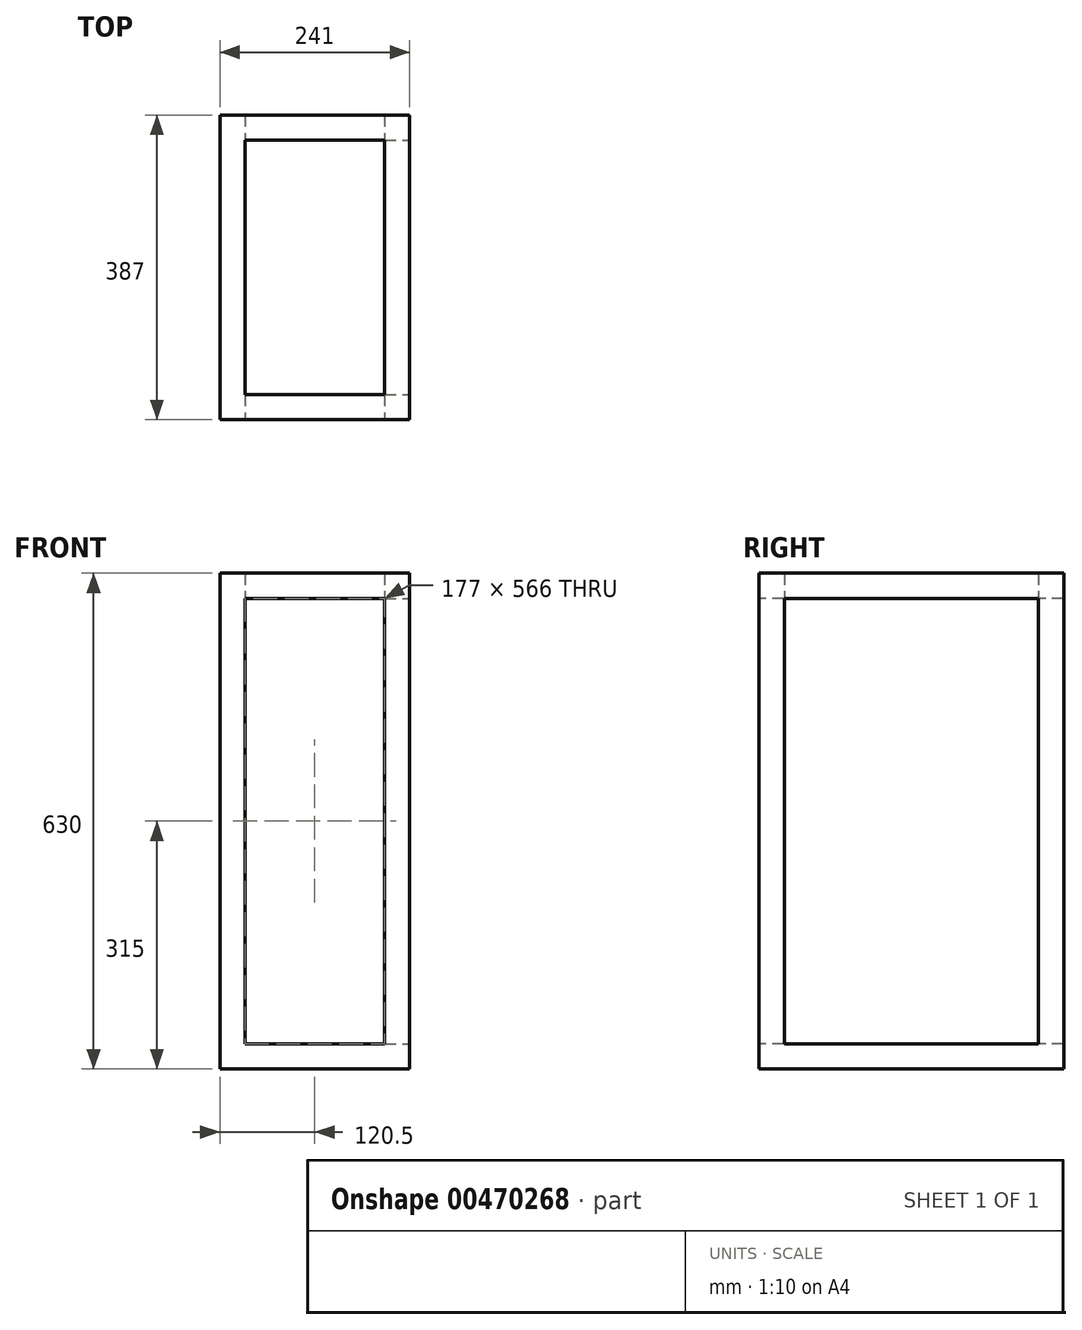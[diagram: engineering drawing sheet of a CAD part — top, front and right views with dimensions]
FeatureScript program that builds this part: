
annotation { "Feature Type Name" : "Feature", "Feature Type Description" : "" }
export const myFeature = defineFeature(function(context is Context, id is Id, definition is map)
    precondition{}
    {
        {
            var Q0;
            Q0=qCreatedBy(makeId("Right.planeOp"),FACE);
            var sketch = newSketch(context, id + "F0", { "sketchPlane" : qUnion([Q0])});
            skLineSegment(sketch, "E0.bottom", {"start": v(193.5, 315) * mm, "end": v(-193.5, 315) * mm});
            skLineSegment(sketch, "E0.top", {"start": v(193.5, -315) * mm, "end": v(-193.5, -315) * mm});
            skLineSegment(sketch, "E0.left", {"start": v(193.5, 315) * mm, "end": v(193.5, -315) * mm});
            skLineSegment(sketch, "E0.right", {"start": v(-193.5, 315) * mm, "end": v(-193.5, -315) * mm});
            skPoint(sketch, "E0.middle", {"position": v(0, 0) * mm});
            skSolve(sketch);
        }
        {
            var Q0;
            Q0=makeQuery(id+"F0.imprint","IMPRINT",FACE,{"disambiguationData":[TD([[makeQuery(id+"F0.imprint","IMPRINT",EDGE,{"derivedFrom":sQuery(id+"F0.wireOp",EDGE,"E0.bottom")}),1.0]])]});
            extrude(context, id + "F1", {"entities" : qUnion([Q0]), "endBound" : BoundingType.SYMMETRIC, "depth" : 241 * mm});
        }
        {
            var Q0;
            Q0=makeQuery(id+"F1.opExtrude","CAP_FACE",FACE,{"disambiguationData":[OSD([sQuery(id+"F0.wireOp",EDGE,"E0.bottom"),sQuery(id+"F0.wireOp",EDGE,"E0.top"),sQuery(id+"F0.wireOp",EDGE,"E0.left"),sQuery(id+"F0.wireOp",EDGE,"E0.right")])],"isStart":false});
            var sketch = newSketch(context, id + "F2", { "sketchPlane" : qUnion([Q0])});
            skLineSegment(sketch, "E1.0", {"start": v(-161.5, -283) * mm, "end": v(161.5, -283) * mm});
            skLineSegment(sketch, "E1.1", {"start": v(-161.5, 283) * mm, "end": v(-161.5, -283) * mm});
            skLineSegment(sketch, "E1.2", {"start": v(161.5, 283) * mm, "end": v(-161.5, 283) * mm});
            skLineSegment(sketch, "E1.3", {"start": v(161.5, -283) * mm, "end": v(161.5, 283) * mm});
            skSolve(sketch);
        }
        {
            var Q0;
            Q0=qCreatedBy(makeId("Top.planeOp"),FACE);
            var sketch = newSketch(context, id + "F3", { "sketchPlane" : qUnion([Q0])});
            skLineSegment(sketch, "E2.0", {"start": v(-88.5, 161.5) * mm, "end": v(-88.5, -161.5) * mm});
            skLineSegment(sketch, "E2.1", {"start": v(88.5, 161.5) * mm, "end": v(-88.5, 161.5) * mm});
            skLineSegment(sketch, "E2.2", {"start": v(88.5, -161.5) * mm, "end": v(88.5, 161.5) * mm});
            skLineSegment(sketch, "E2.3", {"start": v(-88.5, -161.5) * mm, "end": v(88.5, -161.5) * mm});
            skSolve(sketch);
        }
        {
            var Q0;
            Q0=qCreatedBy(makeId("Front.planeOp"),FACE);
            var sketch = newSketch(context, id + "F4", { "sketchPlane" : qUnion([Q0])});
            skLineSegment(sketch, "E3.0", {"start": v(-88.5, -283) * mm, "end": v(-88.5, 283) * mm});
            skLineSegment(sketch, "E3.1", {"start": v(88.5, -283) * mm, "end": v(-88.5, -283) * mm});
            skLineSegment(sketch, "E3.2", {"start": v(88.5, 283) * mm, "end": v(88.5, -283) * mm});
            skLineSegment(sketch, "E3.3", {"start": v(-88.5, 283) * mm, "end": v(88.5, 283) * mm});
            skSolve(sketch);
        }
        {
            var Q0;
            Q0 = qSketchRegion(id + "F3", true);
            extrude(context, id + "F5", {"entities" : qUnion([Q0]), "operationType" : NewBodyOperationType.ADD, "endBound" : BoundingType.SYMMETRIC, "depth" : 291 * mm});
        }
        {
            var Q0;
            Q0=makeQuery(id+"F2.imprint","IMPRINT",FACE,{"disambiguationData":[TD([[makeQuery(id+"F2.imprint","IMPRINT",EDGE,{"derivedFrom":sQuery(id+"F2.wireOp",EDGE,"E1.0")}),1.0]])]});
            extrude(context, id + "F6", {"entities" : qUnion([Q0]), "operationType" : NewBodyOperationType.REMOVE, "oppositeDirection" : true, "depth" : 193 * mm});
        }
        {
            var Q0;
            Q0 = qSketchRegion(id + "F4", true);
            extrude(context, id + "F7", {"entities" : qUnion([Q0]), "operationType" : NewBodyOperationType.REMOVE, "endBound" : BoundingType.SYMMETRIC, "oppositeDirection" : true, "depth" : 422 * mm});
        }
        {
            var Q0;
            Q0=qCreatedBy(makeId("Top.planeOp"),FACE);
            var sketch = newSketch(context, id + "F8", { "sketchPlane" : qUnion([Q0])});
            skLineSegment(sketch, "E4.0", {"start": v(-88.5, 161.5) * mm, "end": v(-88.5, -161.5) * mm});
            skLineSegment(sketch, "E4.1", {"start": v(88.5, 161.5) * mm, "end": v(-88.5, 161.5) * mm});
            skLineSegment(sketch, "E4.2", {"start": v(88.5, -161.5) * mm, "end": v(88.5, 161.5) * mm});
            skLineSegment(sketch, "E4.3", {"start": v(-88.5, -161.5) * mm, "end": v(88.5, -161.5) * mm});
            skSolve(sketch);
        }
        {
            var Q0;
            Q0=makeQuery(id+"F8.imprint","IMPRINT",FACE,{"disambiguationData":[TD([[makeQuery(id+"F8.imprint","IMPRINT",EDGE,{"derivedFrom":sQuery(id+"F8.wireOp",EDGE,"E4.0")}),1.0]])]});
            extrude(context, id + "F9", {"entities" : qUnion([Q0]), "operationType" : NewBodyOperationType.REMOVE, "endBound" : BoundingType.THROUGH_ALL, "depth" : 25 * mm});
        }
    });
